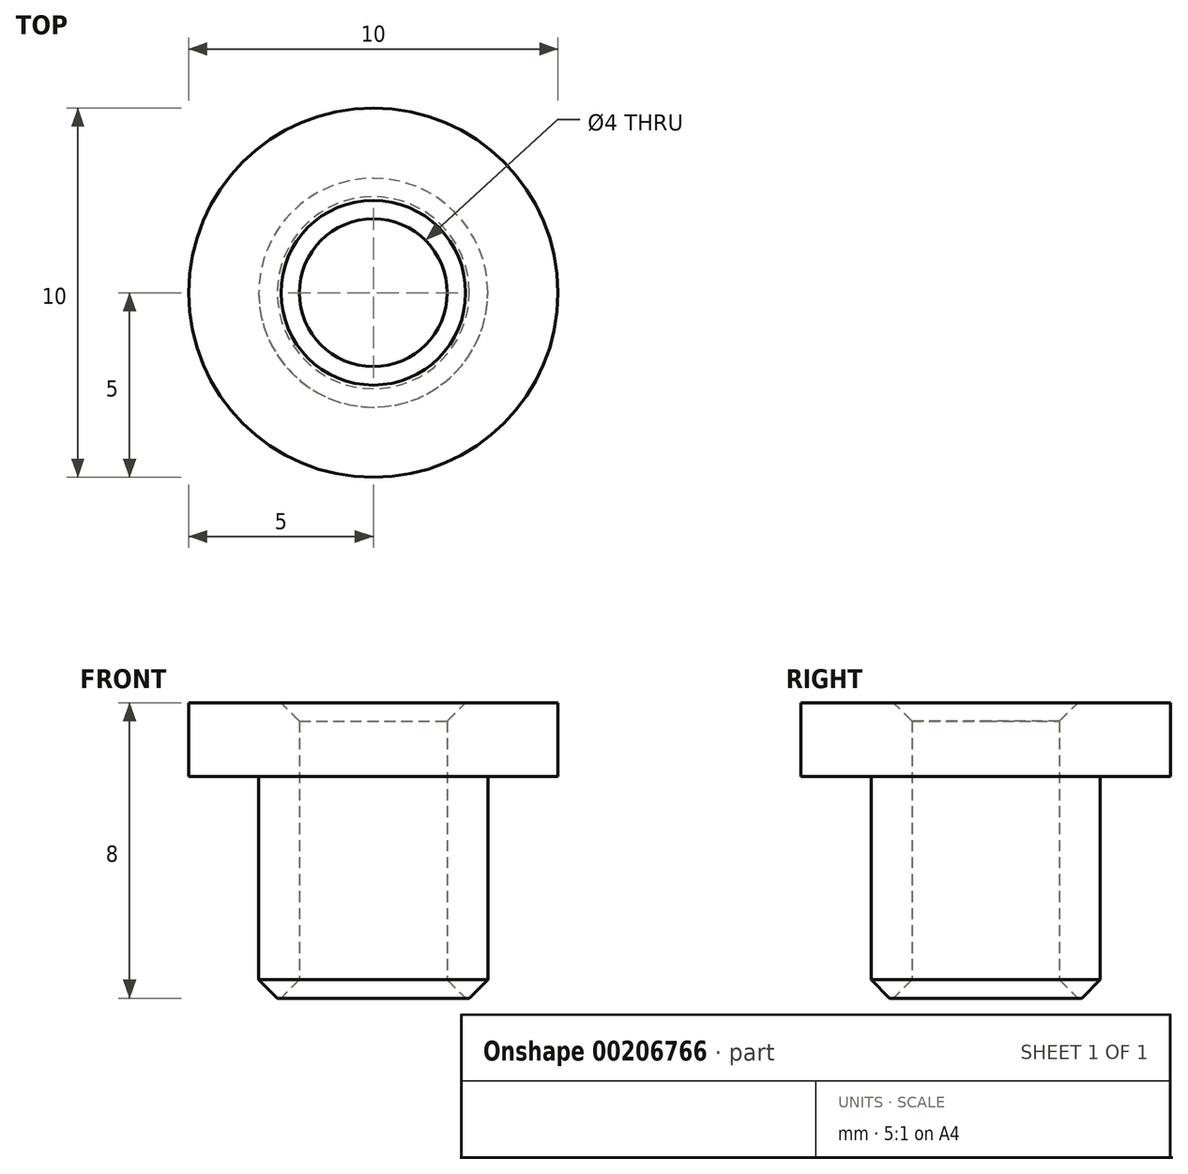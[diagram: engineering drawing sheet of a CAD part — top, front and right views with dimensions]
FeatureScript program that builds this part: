
annotation { "Feature Type Name" : "Feature", "Feature Type Description" : "" }
export const myFeature = defineFeature(function(context is Context, id is Id, definition is map)
    precondition{}
    {
        {
            var Q0;
            Q0=qCreatedBy(makeId("Front.planeOp"),FACE);
            var sketch = newSketch(context, id + "F0", { "sketchPlane" : qUnion([Q0])});
            skLineSegment(sketch, "E0", {"start": v(0, 0) * mm, "end": v(0, 9.9) * mm, "construction": true});
            skLineSegment(sketch, "E1", {"start": v(-2, 0) * mm, "end": v(-2, 8) * mm});
            skLineSegment(sketch, "E2", {"start": v(-2, 8) * mm, "end": v(-5, 8) * mm});
            skLineSegment(sketch, "E3", {"start": v(-3.1, 0) * mm, "end": v(-2, 0) * mm});
            skLineSegment(sketch, "E4", {"start": v(-5, 8) * mm, "end": v(-5, 6) * mm});
            skLineSegment(sketch, "E5", {"start": v(-5, 6) * mm, "end": v(-3.1, 6) * mm});
            skLineSegment(sketch, "E6", {"start": v(-3.1, 6) * mm, "end": v(-3.1, 0) * mm});
            skSolve(sketch);
        }
        {
            var Q0;
            Q0=makeQuery(id+"F0.imprint","IMPRINT",FACE,{"disambiguationData":[TD([[makeQuery(id+"F0.imprint","IMPRINT",EDGE,{"derivedFrom":sQuery(id+"F0.wireOp",EDGE,"E1")}),1.0]])]});
            var Q1;
            Q1=sQuery(id+"F0.wireOp",EDGE,"E0");
            revolve(context, id + "F1", {"entities" : qUnion([Q0]), "axis" : qUnion([Q1]), "revolveType" : RevolveType.FULL});
        }
        {
            var Q0;
            Q0=makeQuery(id+"F1.opRevolve","SWEPT_EDGE",EDGE,{"disambiguationData":[OSD([sQuery(id+"F0.wireOp",EDGE,"E1"),sQuery(id+"F0.wireOp",EDGE,"E2")])]});
            var Q1;
            Q1=makeQuery(id+"F1.opRevolve","SWEPT_EDGE",EDGE,{"disambiguationData":[OSD([sQuery(id+"F0.wireOp",EDGE,"E1"),sQuery(id+"F0.wireOp",EDGE,"E3")])]});
            var Q2;
            Q2=makeQuery(id+"F1.opRevolve","SWEPT_EDGE",EDGE,{"disambiguationData":[OSD([sQuery(id+"F0.wireOp",EDGE,"E3"),sQuery(id+"F0.wireOp",EDGE,"E6")])]});
            chamfer(context, id + "F2", {"entities" : qUnion([Q0, Q1, Q2]), "width" : .5 * mm, "tangentPropagation" : true});
        }
    });
